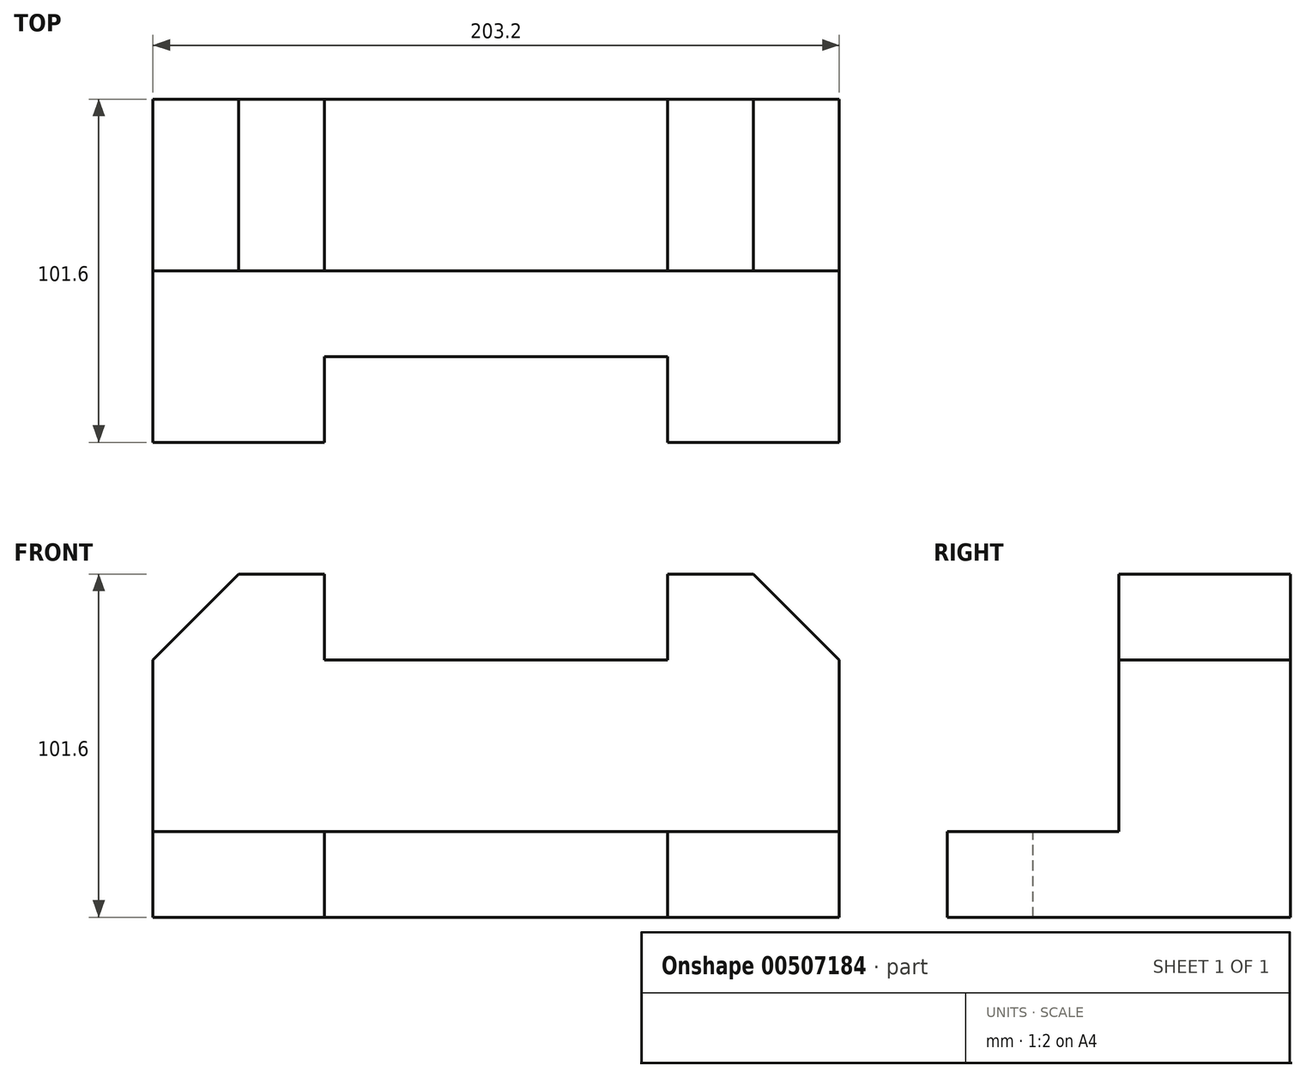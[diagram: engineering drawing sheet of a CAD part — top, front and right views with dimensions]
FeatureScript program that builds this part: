
annotation { "Feature Type Name" : "Feature", "Feature Type Description" : "" }
export const myFeature = defineFeature(function(context is Context, id is Id, definition is map)
    precondition{}
    {
        {
            var Q0;
            Q0=qCreatedBy(makeId("Top.planeOp"),FACE);
            var sketch = newSketch(context, id + "F0", { "sketchPlane" : qUnion([Q0])});
            skLineSegment(sketch, "E0.bottom", {"start": v(0, 0) * mm, "end": v(203.2, 0) * mm});
            skLineSegment(sketch, "E0.top", {"start": v(0, -101.6) * mm, "end": v(203.2, -101.6) * mm});
            skLineSegment(sketch, "E0.left", {"start": v(0, 0) * mm, "end": v(0, -101.6) * mm});
            skLineSegment(sketch, "E0.right", {"start": v(203.2, 0) * mm, "end": v(203.2, -101.6) * mm});
            skSolve(sketch);
        }
        {
            var Q0;
            Q0=makeQuery(id+"F0.imprint","IMPRINT",FACE,{"disambiguationData":[TD([[makeQuery(id+"F0.imprint","IMPRINT",EDGE,{"derivedFrom":sQuery(id+"F0.wireOp",EDGE,"E0.bottom")}),-1.0]])]});
            extrude(context, id + "F1", {"entities" : qUnion([Q0]), "depth" : 101.6 * mm});
        }
        {
            var Q0;
            Q0=makeQuery(id+"F1.opExtrude","CAP_FACE",FACE,{"disambiguationData":[OSD([sQuery(id+"F0.wireOp",EDGE,"E0.bottom"),sQuery(id+"F0.wireOp",EDGE,"E0.top"),sQuery(id+"F0.wireOp",EDGE,"E0.left"),sQuery(id+"F0.wireOp",EDGE,"E0.right")])],"isStart":false});
            var sketch = newSketch(context, id + "F2", { "sketchPlane" : qUnion([Q0])});
            skLineSegment(sketch, "E1.bottom", {"start": v(0, -101.6) * mm, "end": v(203.2, -101.6) * mm});
            skLineSegment(sketch, "E1.top", {"start": v(0, -50.8) * mm, "end": v(203.2, -50.8) * mm});
            skLineSegment(sketch, "E1.left", {"start": v(0, -101.6) * mm, "end": v(0, -50.8) * mm});
            skLineSegment(sketch, "E1.right", {"start": v(203.2, -101.6) * mm, "end": v(203.2, -50.8) * mm});
            skSolve(sketch);
        }
        {
            var Q0;
            Q0=makeQuery(id+"F2.imprint","IMPRINT",FACE,{"disambiguationData":[TD([[makeQuery(id+"F2.imprint","IMPRINT",EDGE,{"derivedFrom":sQuery(id+"F2.wireOp",EDGE,"E1.bottom")}),1.0]])]});
            extrude(context, id + "F3", {"entities" : qUnion([Q0]), "operationType" : NewBodyOperationType.REMOVE, "oppositeDirection" : true, "depth" : 76.2 * mm});
        }
        {
            var Q0;
            Q0=makeQuery(id+"F3.boolean.opBoolean","COPY",FACE,{"derivedFrom":makeQuery(id+"F3.opExtrude","CAP_FACE",FACE,{"disambiguationData":[OSD([sQuery(id+"F2.wireOp",EDGE,"E1.bottom"),sQuery(id+"F2.wireOp",EDGE,"E1.top"),sQuery(id+"F2.wireOp",EDGE,"E1.left"),sQuery(id+"F2.wireOp",EDGE,"E1.right")])],"isStart":false})});
            var sketch = newSketch(context, id + "F4", { "sketchPlane" : qUnion([Q0])});
            skLineSegment(sketch, "E2.bottom", {"start": v(50.8, -101.6) * mm, "end": v(152.4, -101.6) * mm});
            skLineSegment(sketch, "E2.top", {"start": v(50.8, -76.2) * mm, "end": v(152.4, -76.2) * mm});
            skLineSegment(sketch, "E2.left", {"start": v(50.8, -101.6) * mm, "end": v(50.8, -76.2) * mm});
            skLineSegment(sketch, "E2.right", {"start": v(152.4, -101.6) * mm, "end": v(152.4, -76.2) * mm});
            skSolve(sketch);
        }
        {
            var Q0;
            Q0=makeQuery(id+"F4.imprint","IMPRINT",FACE,{"disambiguationData":[TD([[makeQuery(id+"F4.imprint","IMPRINT",EDGE,{"derivedFrom":sQuery(id+"F4.wireOp",EDGE,"E2.bottom")}),1.0]])]});
            extrude(context, id + "F5", {"entities" : qUnion([Q0]), "operationType" : NewBodyOperationType.REMOVE, "oppositeDirection" : true, "depth" : 25.4 * mm});
        }
        {
            var Q0;
            Q0=makeQuery(id+"F1.opExtrude","CAP_FACE",FACE,{"disambiguationData":[OSD([sQuery(id+"F0.wireOp",EDGE,"E0.bottom"),sQuery(id+"F0.wireOp",EDGE,"E0.top"),sQuery(id+"F0.wireOp",EDGE,"E0.left"),sQuery(id+"F0.wireOp",EDGE,"E0.right")])],"isStart":false});
            var sketch = newSketch(context, id + "F6", { "sketchPlane" : qUnion([Q0])});
            skLineSegment(sketch, "E3.bottom", {"start": v(50.8, 0) * mm, "end": v(152.4, 0) * mm});
            skLineSegment(sketch, "E3.top", {"start": v(50.8, -50.8) * mm, "end": v(152.4, -50.8) * mm});
            skLineSegment(sketch, "E3.left", {"start": v(50.8, 0) * mm, "end": v(50.8, -50.8) * mm});
            skLineSegment(sketch, "E3.right", {"start": v(152.4, 0) * mm, "end": v(152.4, -50.8) * mm});
            skSolve(sketch);
        }
        {
            var Q0;
            Q0=makeQuery(id+"F6.imprint","IMPRINT",FACE,{"disambiguationData":[TD([[makeQuery(id+"F6.imprint","IMPRINT",EDGE,{"derivedFrom":sQuery(id+"F6.wireOp",EDGE,"E3.bottom")}),-1.0]])]});
            extrude(context, id + "F7", {"entities" : qUnion([Q0]), "operationType" : NewBodyOperationType.REMOVE, "oppositeDirection" : true, "depth" : 25.4 * mm});
        }
        {
            var Q0;
            Q0=makeQuery(id+"F1.opExtrude","CAP_EDGE",EDGE,{"disambiguationData":[OSD([sQuery(id+"F0.wireOp",EDGE,"E0.right")])],"isStart":false});
            chamfer(context, id + "F8", {"entities" : qUnion([Q0]), "chamferType" : ChamferType.TWO_OFFSETS, "width1" : 25.4 * mm, "oppositeDirection" : false, "width2" : 25.4 * mm, "tangentPropagation" : true});
        }
        {
            var Q0;
            Q0=makeQuery(id+"F1.opExtrude","CAP_EDGE",EDGE,{"disambiguationData":[OSD([sQuery(id+"F0.wireOp",EDGE,"E0.left")])],"isStart":false});
            chamfer(context, id + "F9", {"entities" : qUnion([Q0]), "chamferType" : ChamferType.TWO_OFFSETS, "width1" : 25.4 * mm, "oppositeDirection" : false, "width2" : 25.4 * mm, "tangentPropagation" : true});
        }
    });
